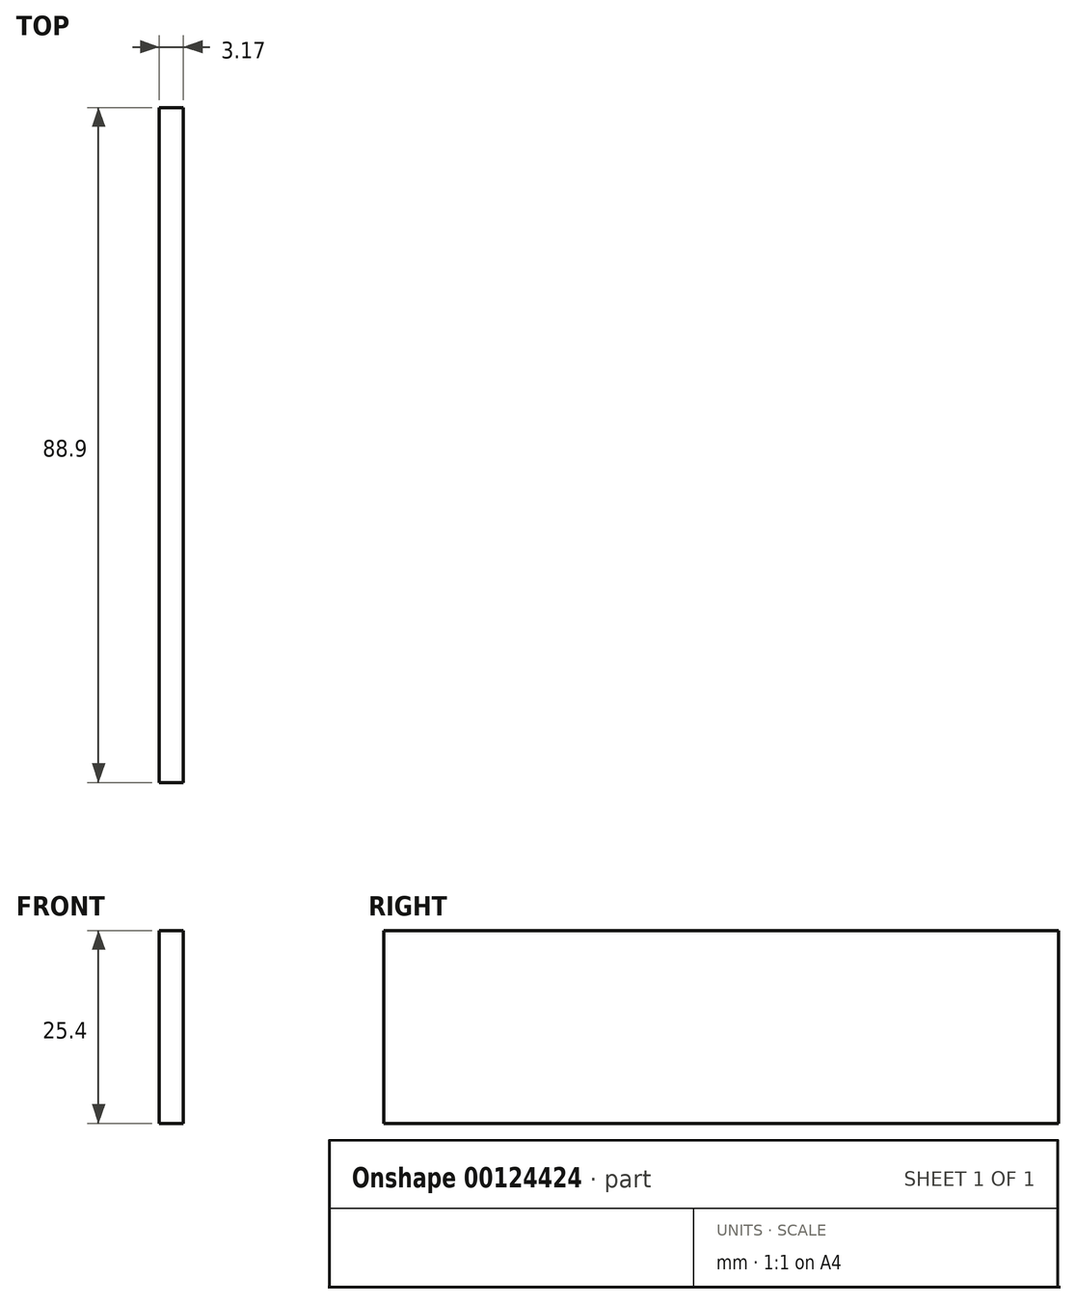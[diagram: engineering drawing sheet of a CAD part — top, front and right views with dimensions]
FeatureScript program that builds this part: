
annotation { "Feature Type Name" : "Feature", "Feature Type Description" : "" }
export const myFeature = defineFeature(function(context is Context, id is Id, definition is map)
    precondition{}
    {
        {
            var Q0;
            Q0=qCreatedBy(makeId("Right.planeOp"),FACE);
            var sketch = newSketch(context, id + "F0", { "sketchPlane" : qUnion([Q0])});
            skLineSegment(sketch, "E0.bottom", {"start": v(44.45, -12.7) * mm, "end": v(-44.45, -12.7) * mm});
            skLineSegment(sketch, "E0.top", {"start": v(44.45, 12.7) * mm, "end": v(-44.45, 12.7) * mm});
            skLineSegment(sketch, "E0.left", {"start": v(44.45, -12.7) * mm, "end": v(44.45, 12.7) * mm});
            skLineSegment(sketch, "E0.right", {"start": v(-44.45, -12.7) * mm, "end": v(-44.45, 12.7) * mm});
            skPoint(sketch, "E0.middle", {"position": v(0, 0) * mm});
            skSolve(sketch);
        }
        {
            var Q0;
            Q0=makeQuery(id+"F0.imprint","IMPRINT",FACE,{"disambiguationData":[TD([[makeQuery(id+"F0.imprint","IMPRINT",EDGE,{"derivedFrom":sQuery(id+"F0.wireOp",EDGE,"E0.bottom")}),-1.0]])]});
            extrude(context, id + "F1", {"entities" : qUnion([Q0]), "depth" : 3.17 * mm});
        }
    });
